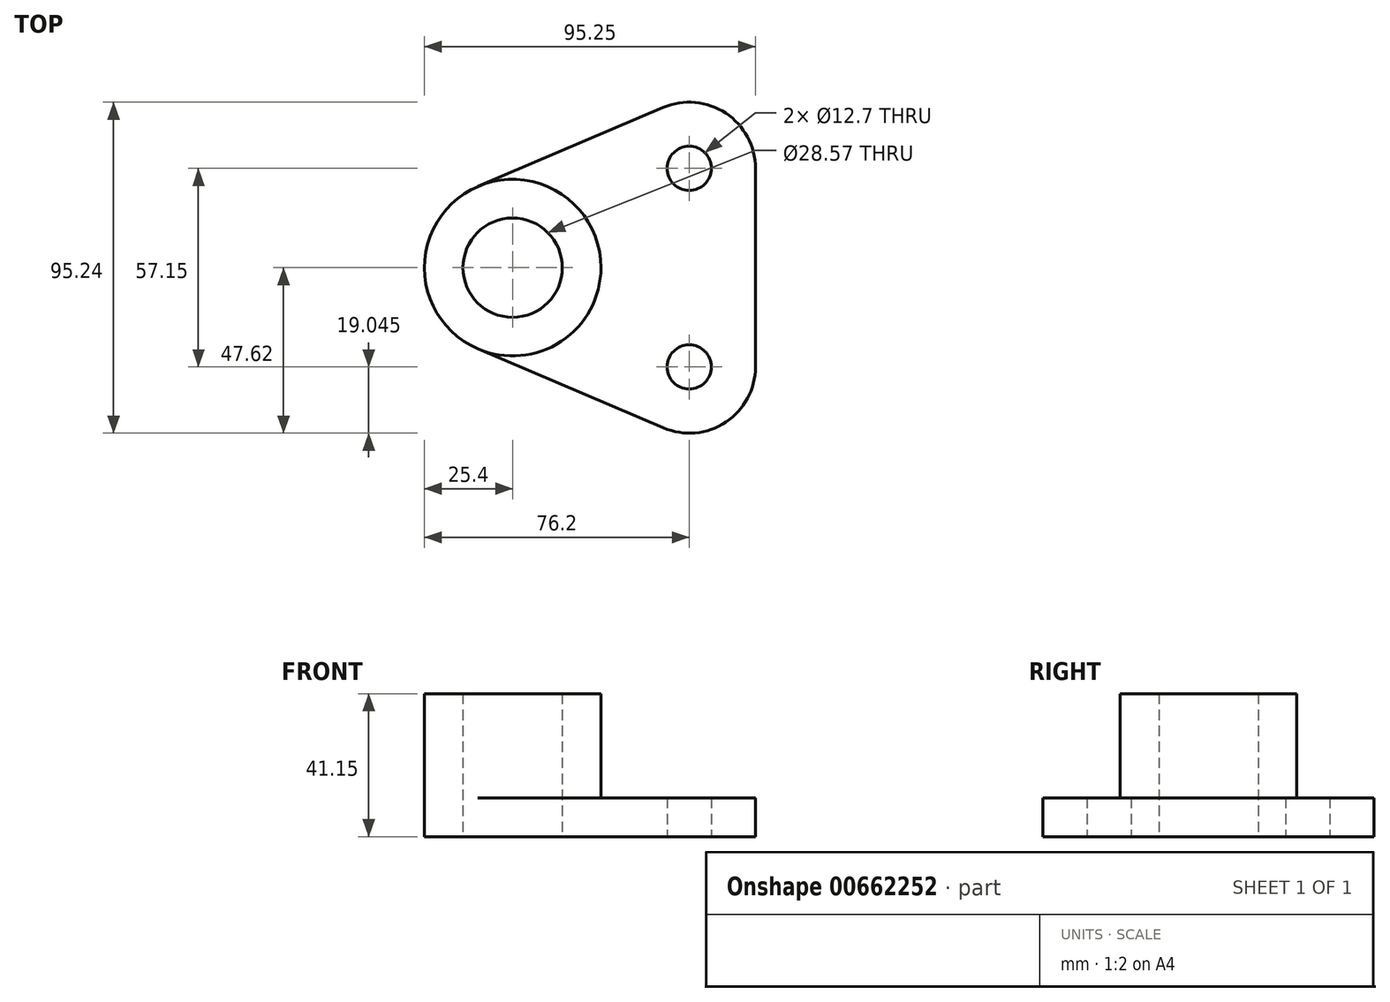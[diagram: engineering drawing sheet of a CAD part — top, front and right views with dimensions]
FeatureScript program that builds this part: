
annotation { "Feature Type Name" : "Feature", "Feature Type Description" : "" }
export const myFeature = defineFeature(function(context is Context, id is Id, definition is map)
    precondition{}
    {
        {
            var Q0;
            Q0=qCreatedBy(makeId("Top.planeOp"),FACE);
            var sketch = newSketch(context, id + "F0", { "sketchPlane" : qUnion([Q0])});
            skCircle(sketch, "E0", {"center": v(-52.37, 0) * mm, "radius": 25.4 * mm});
            skArc(sketch, "E1", {"start": v(17.48, 28.58) * mm, "mid": v(8.93, 44.47) * mm, "end": v(-9.05, 46.1) * mm});
            skArc(sketch, "E2", {"start": v(-9.05, -46.1) * mm, "mid": v(8.93, -44.47) * mm, "end": v(17.48, -28.57) * mm});
            skCircle(sketch, "E3", {"center": v(-1.57, 28.58) * mm, "radius": 6.35 * mm});
            skCircle(sketch, "E4", {"center": v(-1.57, -28.57) * mm, "radius": 6.35 * mm});
            skCircle(sketch, "E5", {"center": v(-52.37, 0) * mm, "radius": 14.29 * mm});
            skLineSegment(sketch, "E6", {"start": v(17.48, 28.58) * mm, "end": v(17.48, -28.57) * mm});
            skLineSegment(sketch, "E7", {"start": v(-62.34, 23.36) * mm, "end": v(-9.05, 46.1) * mm});
            skLineSegment(sketch, "E8", {"start": v(-62.34, -23.36) * mm, "end": v(-9.05, -46.1) * mm});
            skLineSegment(sketch, "E9", {"start": v(-27.17, 3.17) * mm, "end": v(17.48, 3.18) * mm});
            skLineSegment(sketch, "E10", {"start": v(-27.17, -3.18) * mm, "end": v(17.48, -3.17) * mm});
            skSolve(sketch);
        }
        {
            var Q0;
            Q0=makeQuery(id+"F0.imprint","IMPRINT",FACE,{"disambiguationData":[TD([[makeQuery(id+"F0.imprint","IMPRINT",EDGE,{"derivedFrom":sQuery(id+"F0.wireOp",EDGE,"E5")}),-1.0]])]});
            extrude(context, id + "F1", {"entities" : qUnion([Q0]), "depth" : 41.15 * mm, "offsetDistance" : 25.4 * mm});
        }
        {
            var Q0;
            {var subQ1=sQuery(id+"F0.wireOp",EDGE,"E2");Q0=makeQuery(id+"F0.imprint","IMPRINT",FACE,{"disambiguationData":[TD([[makeQuery(id+"F0.imprint","IMPRINT",EDGE,{"derivedFrom":subQ1}),1.0]])]});}
            var Q1;
            {var subQ1=sQuery(id+"F0.wireOp",EDGE,"E1");Q1=makeQuery(id+"F0.imprint","IMPRINT",FACE,{"disambiguationData":[TD([[makeQuery(id+"F0.imprint","IMPRINT",EDGE,{"derivedFrom":subQ1}),1.0]])]});}
            var Q2;
            {var subQ0=sQuery(id+"F0.wireOp",EDGE,"E9");Q2=makeQuery(id+"F0.imprint","IMPRINT",FACE,{"disambiguationData":[TD([[makeQuery(id+"F0.imprint","IMPRINT",EDGE,{"derivedFrom":subQ0}),-1.0]])]});}
            extrude(context, id + "F2", {"entities" : qUnion([Q0, Q1, Q2]), "operationType" : NewBodyOperationType.ADD, "depth" : 11.18 * mm, "offsetDistance" : 25.4 * mm});
        }
    });
